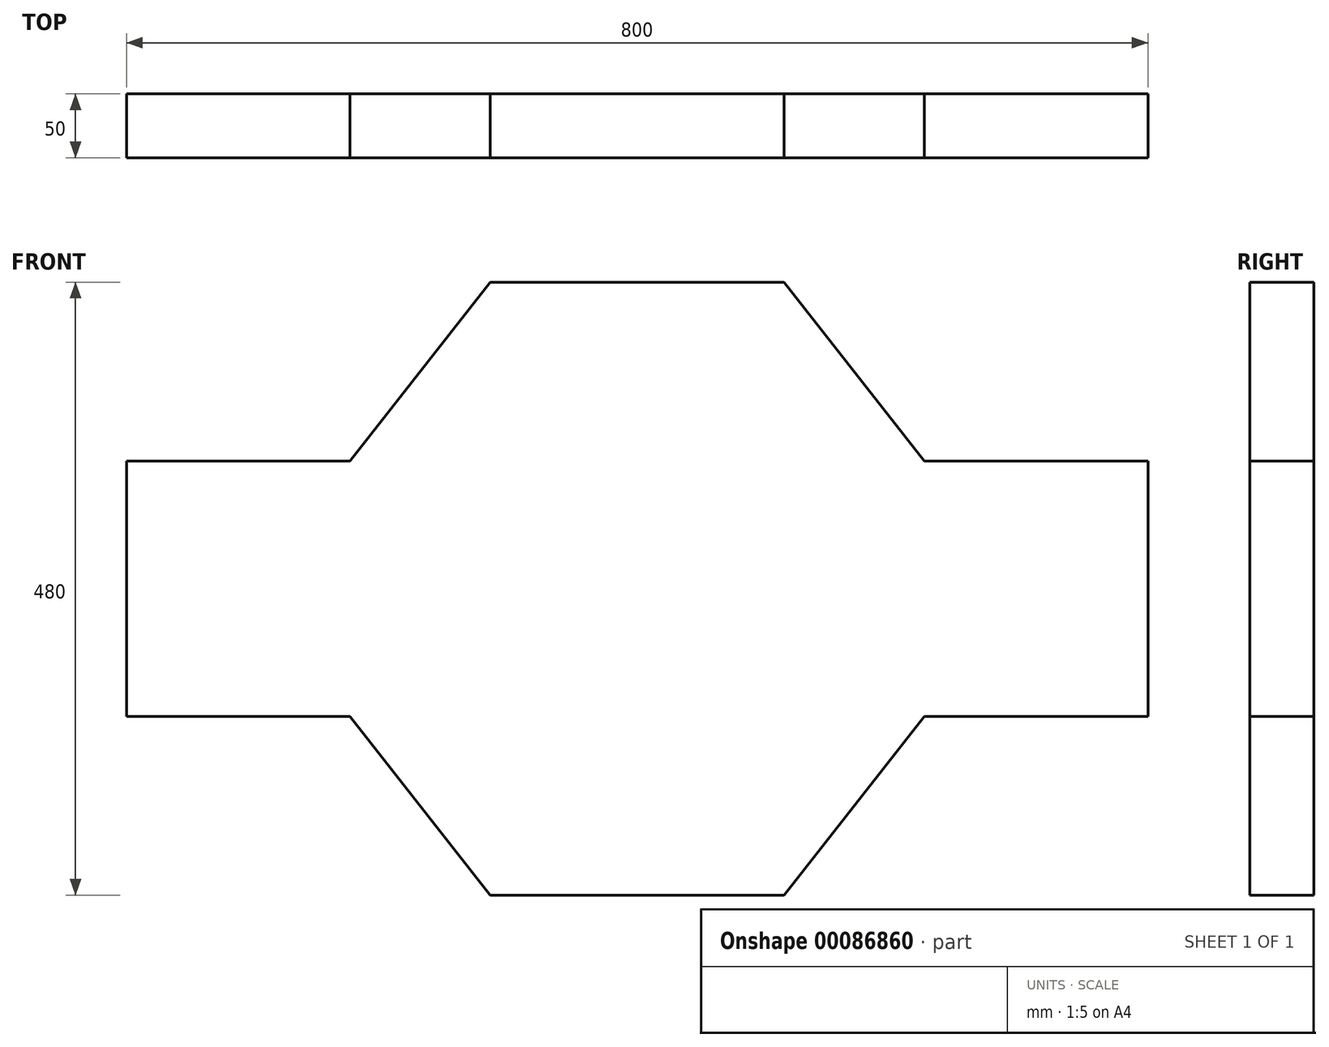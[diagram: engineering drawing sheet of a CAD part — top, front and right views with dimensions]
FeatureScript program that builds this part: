
annotation { "Feature Type Name" : "Feature", "Feature Type Description" : "" }
export const myFeature = defineFeature(function(context is Context, id is Id, definition is map)
    precondition{}
    {
        {
            var Q0;
            Q0=qCreatedBy(makeId("Front.planeOp"),FACE);
            var sketch = newSketch(context, id + "F0", { "sketchPlane" : qUnion([Q0])});
            skLineSegment(sketch, "E0.bottom", {"start": v(-500, 1100) * mm, "end": v(500, 1100) * mm});
            skLineSegment(sketch, "E0.top", {"start": v(-500, -500) * mm, "end": v(500, -500) * mm});
            skLineSegment(sketch, "E0.left", {"start": v(-500, 1100) * mm, "end": v(-500, -500) * mm});
            skLineSegment(sketch, "E0.right", {"start": v(500, 1100) * mm, "end": v(500, -500) * mm});
            skLineSegment(sketch, "E1", {"start": v(0, 0) * mm, "end": v(0, 293.26) * mm, "construction": true});
            skLineSegment(sketch, "E2", {"start": v(0, 0) * mm, "end": v(280.43, 0) * mm, "construction": true});
            skCircle(sketch, "E3", {"center": v(0, 0) * mm, "radius": 200 * mm});
            skLineSegment(sketch, "E4", {"start": v(-400, 0) * mm, "end": v(-400, 100) * mm});
            skLineSegment(sketch, "E5", {"start": v(-400, 100) * mm, "end": v(-225, 100) * mm});
            skLineSegment(sketch, "E6", {"start": v(-225, 100) * mm, "end": v(-115, 240) * mm});
            skLineSegment(sketch, "E7", {"start": v(-115, 240) * mm, "end": v(0, 240) * mm});
            skLineSegment(sketch, "E8.MirrorCS", {"start": v(400, 0) * mm, "end": v(400, 100) * mm});
            skLineSegment(sketch, "E9.MirrorCS", {"start": v(400, 100) * mm, "end": v(225, 100) * mm});
            skLineSegment(sketch, "E10.MirrorCS", {"start": v(225, 100) * mm, "end": v(115, 240) * mm});
            skLineSegment(sketch, "E11.MirrorCS", {"start": v(115, 240) * mm, "end": v(0, 240) * mm});
            skLineSegment(sketch, "E12.MirrorCS", {"start": v(-400, 0) * mm, "end": v(-400, -100) * mm});
            skLineSegment(sketch, "E13.MirrorCS", {"start": v(-400, -100) * mm, "end": v(-225, -100) * mm});
            skLineSegment(sketch, "E14.MirrorCS", {"start": v(-225, -100) * mm, "end": v(-115, -240) * mm});
            skLineSegment(sketch, "E15.MirrorCS", {"start": v(-115, -240) * mm, "end": v(0, -240) * mm});
            skLineSegment(sketch, "E16.MirrorCS", {"start": v(115, -240) * mm, "end": v(0, -240) * mm});
            skLineSegment(sketch, "E17.MirrorCS", {"start": v(225, -100) * mm, "end": v(115, -240) * mm});
            skLineSegment(sketch, "E18.MirrorCS", {"start": v(400, -100) * mm, "end": v(225, -100) * mm});
            skLineSegment(sketch, "E19.MirrorCS", {"start": v(400, 0) * mm, "end": v(400, -100) * mm});
            skSolve(sketch);
        }
        {
            var Q0;
            Q0=makeQuery(id+"F0.imprint","IMPRINT",FACE,{"disambiguationData":[TD([[makeQuery(id+"F0.imprint","IMPRINT",EDGE,{"derivedFrom":sQuery(id+"F0.wireOp",EDGE,"E3")}),-1.0]])]});
            var Q1;
            Q1=makeQuery(id+"F0.imprint","IMPRINT",FACE,{"disambiguationData":[TD([[makeQuery(id+"F0.imprint","IMPRINT",EDGE,{"derivedFrom":sQuery(id+"F0.wireOp",EDGE,"E3")}),1.0]])]});
            extrude(context, id + "F1", {"entities" : qUnion([Q0, Q1]), "depth" : 50 * mm});
        }
    });
